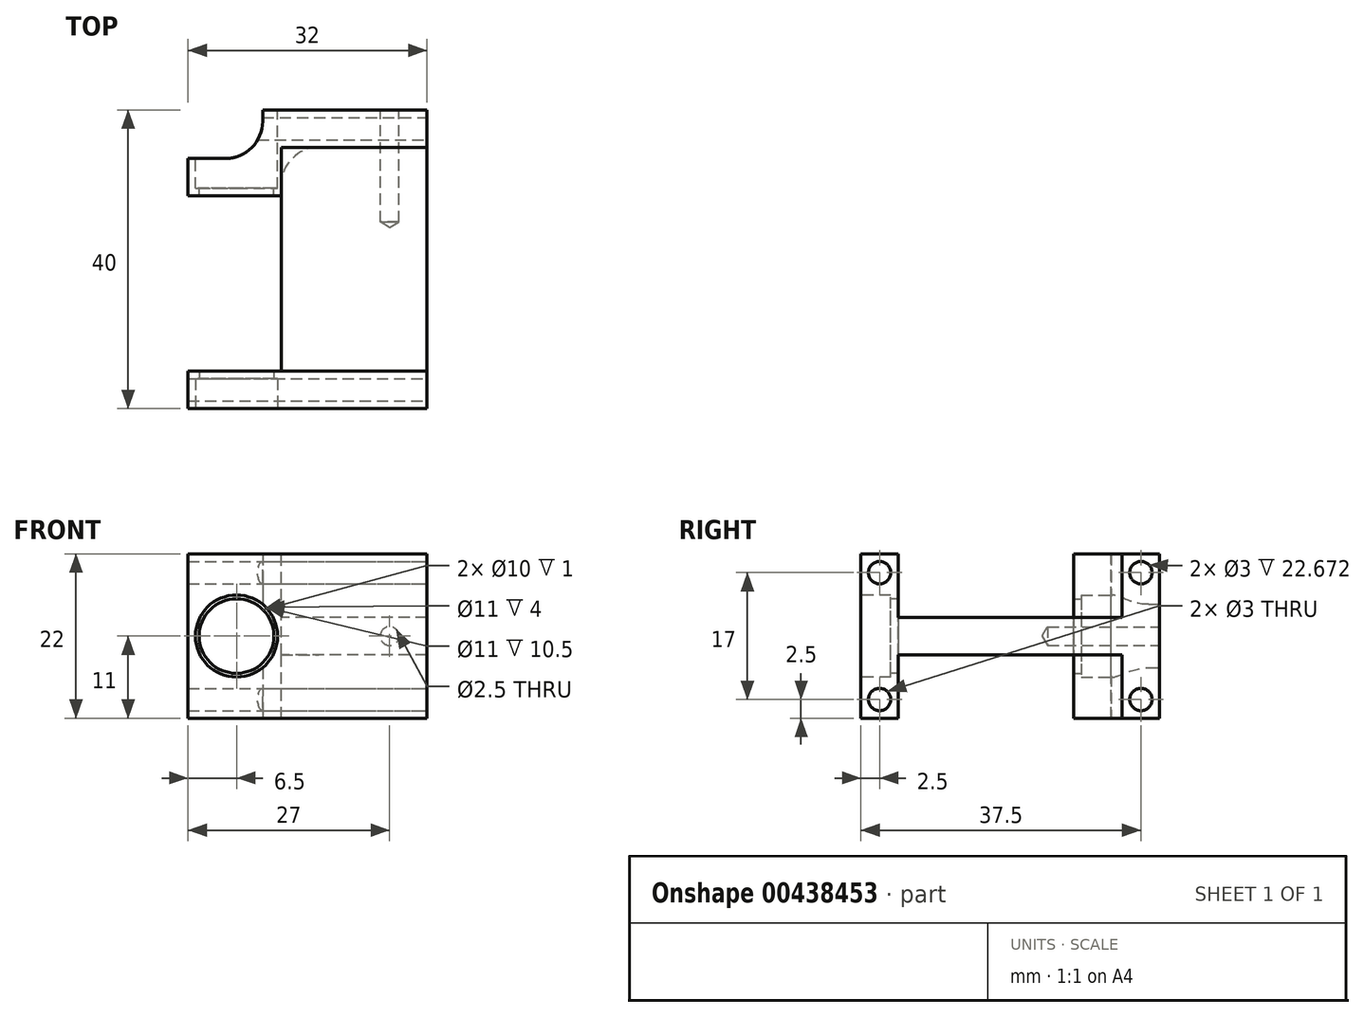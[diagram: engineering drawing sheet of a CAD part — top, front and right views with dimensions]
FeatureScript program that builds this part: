
annotation { "Feature Type Name" : "Feature", "Feature Type Description" : "" }
export const myFeature = defineFeature(function(context is Context, id is Id, definition is map)
    precondition{}
    {
        {
            var Q0;
            Q0=qCreatedBy(makeId("Right.planeOp"),FACE);
            var sketch = newSketch(context, id + "F0", { "sketchPlane" : qUnion([Q0])});
            skLineSegment(sketch, "E0.bottom", {"start": v(20, 2.5) * mm, "end": v(-20, 2.5) * mm});
            skLineSegment(sketch, "E0.top", {"start": v(20, -2.5) * mm, "end": v(-20, -2.5) * mm});
            skLineSegment(sketch, "E0.left", {"start": v(20, 2.5) * mm, "end": v(20, -2.5) * mm});
            skLineSegment(sketch, "E0.right", {"start": v(-20, 2.5) * mm, "end": v(-20, -2.5) * mm});
            skPoint(sketch, "E0.middle", {"position": v(0, 0) * mm});
            skLineSegment(sketch, "E1.bottom", {"start": v(-20, 11) * mm, "end": v(-15, 11) * mm});
            skLineSegment(sketch, "E1.top", {"start": v(-20, -11) * mm, "end": v(-15, -11) * mm});
            skLineSegment(sketch, "E1.left", {"start": v(-20, 11) * mm, "end": v(-20, -11) * mm});
            skLineSegment(sketch, "E1.right", {"start": v(-15, 11) * mm, "end": v(-15, -11) * mm});
            skPoint(sketch, "E2", {"position": v(-20, 0) * mm});
            skPoint(sketch, "E3.MirrorP", {"position": v(20, 0) * mm});
            skLineSegment(sketch, "E4.MirrorCS", {"start": v(15, 11) * mm, "end": v(15, -11) * mm});
            skLineSegment(sketch, "E5.MirrorCS", {"start": v(20, 11) * mm, "end": v(20, -11) * mm});
            skLineSegment(sketch, "E6.MirrorCS", {"start": v(20, 11) * mm, "end": v(15, 11) * mm});
            skLineSegment(sketch, "E7.MirrorCS", {"start": v(20, -11) * mm, "end": v(15, -11) * mm});
            skPoint(sketch, "E8", {"position": v(-17.5, 8.5) * mm});
            skPoint(sketch, "E9", {"position": v(-17.5, 11) * mm});
            skPoint(sketch, "E10.MirrorP", {"position": v(-17.5, -8.5) * mm});
            skPoint(sketch, "E11.MirrorP", {"position": v(17.5, 8.5) * mm});
            skPoint(sketch, "E12.MirrorP", {"position": v(17.5, -8.5) * mm});
            skSolve(sketch);
        }
        {
            var Q0;
            Q0 = qSketchRegion(id + "F0", true);
            extrude(context, id + "F1", {"entities" : qUnion([Q0]), "depth" : 30 * mm});
        }
        {
            var Q0;
            {var subQ5=sQuery(id+"F0.wireOp",EDGE,"E1.bottom");Q0=makeQuery(id+"F0.imprint","IMPRINT",FACE,{"disambiguationData":[TD([[makeQuery(id+"F0.imprint","IMPRINT",EDGE,{"derivedFrom":subQ5}),-1.0]])]});}
            var Q1;
            {var subQ0=sQuery(id+"F0.wireOp",EDGE,"E1.left");var subQ1=sQuery(id+"F0.wireOp",EDGE,"E0.bottom");var subQ2=makeQuery(id+"F0.imprint","INTERSECT",VERTEX,{"derivedFrom":[subQ1,subQ0]});Q1=makeQuery(id+"F0.imprint","IMPRINT",FACE,{"disambiguationData":[TD([[makeQuery(id+"F0.imprint","IMPRINT",EDGE,{"disambiguationData":[TD([[subQ2,1.0]])],"derivedFrom":subQ1}),1.0]])]});}
            var Q2;
            {var subQ5=sQuery(id+"F0.wireOp",EDGE,"E1.top");Q2=makeQuery(id+"F0.imprint","IMPRINT",FACE,{"disambiguationData":[TD([[makeQuery(id+"F0.imprint","IMPRINT",EDGE,{"derivedFrom":subQ5}),1.0]])]});}
            extrude(context, id + "F2", {"entities" : qUnion([Q0, Q1, Q2]), "operationType" : NewBodyOperationType.ADD, "oppositeDirection" : true, "depth" : 2 * mm});
        }
        {
            var Q0;
            Q0=makeQuery(id+"F1.opExtrude","SWEPT_FACE",FACE,{"disambiguationData":[OSD([sQuery(id+"F0.wireOp",EDGE,"E1.left")])]});
            var sketch = newSketch(context, id + "F3", { "sketchPlane" : qUnion([Q0])});
            skCircle(sketch, "E13", {"center": v(4.5, 0) * mm, "radius": 2.5 * mm});
            skCircle(sketch, "E14", {"center": v(4.5, 0) * mm, "radius": 5.5 * mm});
            skCircle(sketch, "E15.0", {"center": v(4.5, 0) * mm, "radius": 5 * mm});
            skSolve(sketch);
        }
        {
            var Q0;
            Q0=makeQuery(id+"F1.opExtrude","SWEPT_FACE",FACE,{"disambiguationData":[OSD([sQuery(id+"F0.wireOp",EDGE,"E0.bottom")])]});
            var sketch = newSketch(context, id + "F4", { "sketchPlane" : qUnion([Q0])});
            skLineSegment(sketch, "E16", {"start": v(4.5, 15) * mm, "end": v(4.5, -15) * mm, "construction": true});
            skLineSegment(sketch, "E17", {"start": v(10.5, 15) * mm, "end": v(10.5, -15) * mm});
            skLineSegment(sketch, "E18", {"start": v(0, 0) * mm, "end": v(30, 0) * mm, "construction": true});
            skSolve(sketch);
        }
        {
            var Q0;
            {var subQ0=sQuery(id+"F4.wireOp",EDGE,"E17");Q0=makeQuery(id+"F4.imprint","IMPRINT",FACE,{"disambiguationData":[TD([[makeQuery(id+"F4.imprint","IMPRINT",EDGE,{"derivedFrom":subQ0}),-1.0]])]});}
            extrude(context, id + "F5", {"entities" : qUnion([Q0]), "operationType" : NewBodyOperationType.REMOVE, "endBound" : BoundingType.THROUGH_ALL, "oppositeDirection" : true, "depth" : 25 * mm});
        }
        {
            var Q0;
            Q0=makeQuery(id+"F3.imprint","IMPRINT",FACE,{"disambiguationData":[TD([[makeQuery(id+"F3.imprint","IMPRINT",EDGE,{"derivedFrom":sQuery(id+"F3.wireOp",EDGE,"E13")}),-1.0]])]});
            var Q1;
            Q1=makeQuery(id+"F3.imprint","IMPRINT",FACE,{"disambiguationData":[TD([[makeQuery(id+"F3.imprint","IMPRINT",EDGE,{"derivedFrom":sQuery(id+"F3.wireOp",EDGE,"E13")}),1.0]])]});
            var Q2;
            Q2=makeQuery(id+"F3.imprint","IMPRINT",FACE,{"disambiguationData":[TD([[makeQuery(id+"F3.imprint","IMPRINT",EDGE,{"derivedFrom":sQuery(id+"F3.wireOp",EDGE,"E14")}),1.0]])]});
            extrude(context, id + "F6", {"entities" : qUnion([Q0, Q1, Q2]), "operationType" : NewBodyOperationType.REMOVE, "oppositeDirection" : true, "depth" : 4 * mm});
        }
        {
            var Q0;
            Q0=makeQuery(id+"F3.imprint","IMPRINT",FACE,{"disambiguationData":[TD([[makeQuery(id+"F3.imprint","IMPRINT",EDGE,{"derivedFrom":sQuery(id+"F3.wireOp",EDGE,"E13")}),1.0]])]});
            var Q1;
            Q1=makeQuery(id+"F3.imprint","IMPRINT",FACE,{"disambiguationData":[TD([[makeQuery(id+"F3.imprint","IMPRINT",EDGE,{"derivedFrom":sQuery(id+"F3.wireOp",EDGE,"E13")}),-1.0]])]});
            var Q2;
            {var subQ0=sQuery(id+"F0.wireOp",EDGE,"E1.right");var subQ1=sQuery(id+"F0.wireOp",EDGE,"E0.bottom");Q2=makeQuery(id+"F5.boolean.opBoolean","MERGE",FACE,{"derivedFrom":[makeQuery(id+"F2.boolean.opBoolean","MERGE",FACE,{"derivedFrom":[makeQuery(id+"F1.opExtrude","SWEPT_FACE",FACE,{"disambiguationData":[OSD([subQ0]),TDD([makeQuery(id+"F0.imprint","IMPRINT",EDGE,{"disambiguationData":[TD([[makeQuery(id+"F0.imprint","INTERSECT",VERTEX,{"derivedFrom":[sQuery(id+"F0.wireOp",EDGE,"E1.bottom"),subQ0]}),-1.0]])],"derivedFrom":subQ0})])]}),makeQuery(id+"F1.opExtrude","SWEPT_FACE",FACE,{"disambiguationData":[OSD([subQ0]),TDD([makeQuery(id+"F0.imprint","IMPRINT",EDGE,{"disambiguationData":[TD([[makeQuery(id+"F0.imprint","INTERSECT",VERTEX,{"derivedFrom":[sQuery(id+"F0.wireOp",EDGE,"E1.top"),subQ0]}),1.0]])],"derivedFrom":subQ0})])]}),makeQuery(id+"F2.opExtrude","SWEPT_FACE",FACE,{"disambiguationData":[OSD([subQ0])]})]}),makeQuery(id+"F5.opExtrude","SWEPT_FACE",FACE,{"disambiguationData":[OSD([subQ1,subQ0])]})]});}
            extrude(context, id + "F7", {"entities" : qUnion([Q0, Q1]), "operationType" : NewBodyOperationType.REMOVE, "endBound" : BoundingType.UP_TO_SURFACE, "oppositeDirection" : true, "endBoundEntityFace" : qUnion([Q2]), "depth" : 25 * mm});
        }
        {
            var Q0;
            Q0=makeQuery(id+"F1.opExtrude","SWEPT_FACE",FACE,{"disambiguationData":[OSD([sQuery(id+"F0.wireOp",EDGE,"E6.MirrorCS")])]});
            var sketch = newSketch(context, id + "F8", { "sketchPlane" : qUnion([Q0])});
            skLineSegment(sketch, "E19.bottom", {"start": v(10.5, 15) * mm, "end": v(-2, 15) * mm});
            skLineSegment(sketch, "E19.top", {"start": v(10.5, 8.5) * mm, "end": v(-2, 8.5) * mm});
            skLineSegment(sketch, "E19.left", {"start": v(10.5, 15) * mm, "end": v(10.5, 8.5) * mm});
            skLineSegment(sketch, "E19.right", {"start": v(-2, 15) * mm, "end": v(-2, 8.5) * mm});
            skSolve(sketch);
        }
        {
            var Q0;
            Q0=makeQuery(id+"F8.imprint","IMPRINT",FACE,{"disambiguationData":[TD([[makeQuery(id+"F8.imprint","IMPRINT",EDGE,{"derivedFrom":sQuery(id+"F8.wireOp",EDGE,"E19.top")}),-1.0]])]});
            var Q1;
            Q1=makeQuery(id+"F1.opExtrude","SWEPT_FACE",FACE,{"disambiguationData":[OSD([sQuery(id+"F0.wireOp",EDGE,"E7.MirrorCS")])]});
            extrude(context, id + "F9", {"entities" : qUnion([Q0]), "operationType" : NewBodyOperationType.ADD, "endBound" : BoundingType.UP_TO_SURFACE, "oppositeDirection" : true, "endBoundEntityFace" : qUnion([Q1]), "depth" : 25 * mm});
        }
        {
            var Q0;
            Q0=makeQuery(id+"F1.opExtrude","CAP_FACE",FACE,{"disambiguationData":[OSD([sQuery(id+"F0.wireOp",EDGE,"E0.bottom"),sQuery(id+"F0.wireOp",EDGE,"E0.top"),sQuery(id+"F0.wireOp",EDGE,"E1.bottom"),sQuery(id+"F0.wireOp",EDGE,"E1.top"),sQuery(id+"F0.wireOp",EDGE,"E1.left"),sQuery(id+"F0.wireOp",EDGE,"E1.right"),sQuery(id+"F0.wireOp",EDGE,"E4.MirrorCS"),sQuery(id+"F0.wireOp",EDGE,"E5.MirrorCS"),sQuery(id+"F0.wireOp",EDGE,"E6.MirrorCS"),sQuery(id+"F0.wireOp",EDGE,"E7.MirrorCS")])],"isStart":true});
            extrude(context, id + "F10", {"entities" : qUnion([Q0]), "operationType" : NewBodyOperationType.REMOVE, "oppositeDirection" : true, "depth" : 8 * mm});
        }
        {
            var Q0;
            Q0=makeQuery(id+"F10.boolean.opBoolean","MERGE",FACE,{"derivedFrom":[makeQuery(id+"F9.opExtrude","SWEPT_FACE",FACE,{"disambiguationData":[OSD([sQuery(id+"F8.wireOp",EDGE,"E19.bottom")])]}),makeQuery(id+"F10.opExtrude","SWEPT_FACE",FACE,{"disambiguationData":[OSD([sQuery(id+"F0.wireOp",EDGE,"E0.bottom"),sQuery(id+"F0.wireOp",EDGE,"E4.MirrorCS")])]})]});
            extrude(context, id + "F11", {"entities" : qUnion([Q0]), "operationType" : NewBodyOperationType.REMOVE, "oppositeDirection" : true, "depth" : 1.5 * mm});
        }
        {
            var Q0;
            Q0=makeQuery(id+"F11.boolean.opBoolean","COPY",EDGE,{"derivedFrom":makeQuery(id+"F11.opExtrude","CAP_EDGE",EDGE,{"disambiguationData":[OSD([sQuery(id+"F0.wireOp",EDGE,"E0.bottom"),sQuery(id+"F0.wireOp",EDGE,"E4.MirrorCS")])],"isStart":false})});
            fillet(context, id + "F12", {"entities" : qUnion([Q0]), "radius" : 5 * mm, "tangentPropagation" : true, "allowEdgeOverflow" : false});
        }
        {
            var Q0;
            {var subQ0=sQuery(id+"F0.wireOp",EDGE,"E6.MirrorCS");var subQ1=sQuery(id+"F0.wireOp",EDGE,"E4.MirrorCS");var subQ2=sQuery(id+"F0.wireOp",EDGE,"E0.bottom");var subQ3=sQuery(id+"F8.wireOp",EDGE,"E19.left");var subQ4=sQuery(id+"F8.wireOp",EDGE,"E19.bottom");Q0=makeQuery(id+"F9.boolean.opBoolean","SPLIT",EDGE,{"disambiguationData":[TD([makeQuery(id+"F1.opExtrude","SWEPT_FACE",FACE,{"disambiguationData":[OSD([subQ2])]})])],"derivedFrom":makeQuery(id+"F9.opExtrude","SWEPT_EDGE",EDGE,{"disambiguationData":[OSD([subQ1,subQ0,subQ4,subQ3])]})});}
            var Q1;
            {var subQ1=sQuery(id+"F0.wireOp",EDGE,"E4.MirrorCS");var subQ2=sQuery(id+"F0.wireOp",EDGE,"E0.top");var subQ4=sQuery(id+"F0.wireOp",EDGE,"E6.MirrorCS");var subQ5=sQuery(id+"F8.wireOp",EDGE,"E19.left");Q1=makeQuery(id+"F9.boolean.opBoolean","SPLIT",EDGE,{"disambiguationData":[TD([makeQuery(id+"F1.opExtrude","SWEPT_FACE",FACE,{"disambiguationData":[OSD([subQ2])]})])],"derivedFrom":makeQuery(id+"F9.opExtrude","SWEPT_EDGE",EDGE,{"disambiguationData":[OSD([subQ1,subQ4,sQuery(id+"F8.wireOp",EDGE,"E19.bottom"),subQ5])]})});}
            fillet(context, id + "F13", {"entities" : qUnion([Q0, Q1]), "radius" : 5 * mm, "tangentPropagation" : true, "allowEdgeOverflow" : false});
        }
        {
            var Q0;
            Q0=makeQuery(id+"F1.opExtrude","SWEPT_FACE",FACE,{"disambiguationData":[OSD([sQuery(id+"F0.wireOp",EDGE,"E5.MirrorCS")])]});
            var sketch = newSketch(context, id + "F14", { "sketchPlane" : qUnion([Q0])});
            skCircle(sketch, "E20", {"center": v(-4.5, 0) * mm, "radius": 2.5 * mm});
            skCircle(sketch, "E21", {"center": v(-4.5, 0) * mm, "radius": 5.5 * mm});
            skCircle(sketch, "E22.0", {"center": v(-4.5, 0) * mm, "radius": 5 * mm});
            skSolve(sketch);
        }
        {
            var Q0;
            {var subQ0=sQuery(id+"F14.wireOp",EDGE,"E21");var subQ1=makeQuery(id+"F10.boolean.opBoolean","COPY",EDGE,{"derivedFrom":makeQuery(id+"F10.opExtrude","CAP_EDGE",EDGE,{"disambiguationData":[OSD([sQuery(id+"F0.wireOp",EDGE,"E5.MirrorCS")])],"isStart":false})});var subQ2=makeQuery(id+"F14.imprint","INTERSECT",VERTEX,{"disambiguationData":[OD(0.0)],"derivedFrom":[subQ1,subQ0]});Q0=makeQuery(id+"F14.imprint","IMPRINT",FACE,{"disambiguationData":[TD([[makeQuery(id+"F14.imprint","IMPRINT",EDGE,{"disambiguationData":[TD([[subQ2,-1.0]])],"derivedFrom":subQ0}),1.0]])]});}
            var Q1;
            {var subQ0=sQuery(id+"F14.wireOp",EDGE,"E21");var subQ1=makeQuery(id+"F10.boolean.opBoolean","COPY",EDGE,{"derivedFrom":makeQuery(id+"F10.opExtrude","CAP_EDGE",EDGE,{"disambiguationData":[OSD([sQuery(id+"F0.wireOp",EDGE,"E5.MirrorCS")])],"isStart":false})});var subQ2=makeQuery(id+"F14.imprint","INTERSECT",VERTEX,{"disambiguationData":[OD(0.0)],"derivedFrom":[subQ1,subQ0]});Q1=makeQuery(id+"F14.imprint","IMPRINT",FACE,{"disambiguationData":[TD([[makeQuery(id+"F14.imprint","IMPRINT",EDGE,{"disambiguationData":[TD([[subQ2,1.0]])],"derivedFrom":subQ0}),1.0]])]});}
            var Q2;
            {var subQ0=sQuery(id+"F14.wireOp",EDGE,"E20");var subQ1=makeQuery(id+"F10.boolean.opBoolean","COPY",EDGE,{"derivedFrom":makeQuery(id+"F10.opExtrude","CAP_EDGE",EDGE,{"disambiguationData":[OSD([sQuery(id+"F0.wireOp",EDGE,"E5.MirrorCS")])],"isStart":false})});var subQ2=makeQuery(id+"F14.imprint","INTERSECT",VERTEX,{"disambiguationData":[OD(0.0)],"derivedFrom":[subQ1,subQ0]});Q2=makeQuery(id+"F14.imprint","IMPRINT",FACE,{"disambiguationData":[TD([[makeQuery(id+"F14.imprint","IMPRINT",EDGE,{"disambiguationData":[TD([[subQ2,-1.0]])],"derivedFrom":subQ0}),-1.0]])]});}
            var Q3;
            {var subQ0=sQuery(id+"F14.wireOp",EDGE,"E20");var subQ1=makeQuery(id+"F10.boolean.opBoolean","COPY",EDGE,{"derivedFrom":makeQuery(id+"F10.opExtrude","CAP_EDGE",EDGE,{"disambiguationData":[OSD([sQuery(id+"F0.wireOp",EDGE,"E5.MirrorCS")])],"isStart":false})});var subQ2=makeQuery(id+"F14.imprint","INTERSECT",VERTEX,{"disambiguationData":[OD(0.0)],"derivedFrom":[subQ1,subQ0]});Q3=makeQuery(id+"F14.imprint","IMPRINT",FACE,{"disambiguationData":[TD([[makeQuery(id+"F14.imprint","IMPRINT",EDGE,{"disambiguationData":[TD([[subQ2,-1.0]])],"derivedFrom":subQ0}),1.0]])]});}
            var Q4;
            {var subQ0=sQuery(id+"F14.wireOp",EDGE,"E20");var subQ1=makeQuery(id+"F10.boolean.opBoolean","COPY",EDGE,{"derivedFrom":makeQuery(id+"F10.opExtrude","CAP_EDGE",EDGE,{"disambiguationData":[OSD([sQuery(id+"F0.wireOp",EDGE,"E5.MirrorCS")])],"isStart":false})});var subQ2=makeQuery(id+"F14.imprint","INTERSECT",VERTEX,{"disambiguationData":[OD(0.0)],"derivedFrom":[subQ1,subQ0]});Q4=makeQuery(id+"F14.imprint","IMPRINT",FACE,{"disambiguationData":[TD([[makeQuery(id+"F14.imprint","IMPRINT",EDGE,{"disambiguationData":[TD([[subQ2,1.0]])],"derivedFrom":subQ0}),1.0]])]});}
            var Q5;
            {var subQ0=sQuery(id+"F14.wireOp",EDGE,"E20");var subQ1=makeQuery(id+"F10.boolean.opBoolean","COPY",EDGE,{"derivedFrom":makeQuery(id+"F10.opExtrude","CAP_EDGE",EDGE,{"disambiguationData":[OSD([sQuery(id+"F0.wireOp",EDGE,"E5.MirrorCS")])],"isStart":false})});var subQ2=makeQuery(id+"F14.imprint","INTERSECT",VERTEX,{"disambiguationData":[OD(0.0)],"derivedFrom":[subQ1,subQ0]});Q5=makeQuery(id+"F14.imprint","IMPRINT",FACE,{"disambiguationData":[TD([[makeQuery(id+"F14.imprint","IMPRINT",EDGE,{"disambiguationData":[TD([[subQ2,1.0]])],"derivedFrom":subQ0}),-1.0]])]});}
            extrude(context, id + "F15", {"entities" : qUnion([Q0, Q1, Q2, Q3, Q4, Q5]), "operationType" : NewBodyOperationType.REMOVE, "oppositeDirection" : true, "depth" : 10.5 * mm});
        }
        {
            var Q0;
            {var subQ0=sQuery(id+"F14.wireOp",EDGE,"E22.0");var subQ1=makeQuery(id+"F12.opFillet","BLEND_EDGE",EDGE,{"blendedFrom":[makeQuery(id+"F10.boolean.opBoolean","COPY",EDGE,{"derivedFrom":makeQuery(id+"F10.opExtrude","CAP_EDGE",EDGE,{"disambiguationData":[OSD([sQuery(id+"F0.wireOp",EDGE,"E0.bottom"),sQuery(id+"F0.wireOp",EDGE,"E4.MirrorCS")])],"isStart":false})}),makeQuery(id+"F1.opExtrude","SWEPT_FACE",FACE,{"disambiguationData":[OSD([sQuery(id+"F0.wireOp",EDGE,"E5.MirrorCS")])]})],"blendedInto":[makeQuery(id+"F1.opExtrude","SWEPT_FACE",FACE,{"disambiguationData":[OSD([sQuery(id+"F0.wireOp",EDGE,"E5.MirrorCS")])]})]});var subQ2=makeQuery(id+"F14.imprint","INTERSECT",VERTEX,{"disambiguationData":[OD(0.0)],"derivedFrom":[subQ1,subQ0]});Q0=makeQuery(id+"F14.imprint","IMPRINT",FACE,{"disambiguationData":[TD([[makeQuery(id+"F14.imprint","IMPRINT",EDGE,{"disambiguationData":[TD([[subQ2,-1.0]])],"derivedFrom":subQ0}),1.0]])]});}
            var Q1;
            Q1=makeQuery(id+"F14.imprint","IMPRINT",FACE,{"disambiguationData":[TD([[makeQuery(id+"F14.imprint","IMPRINT",EDGE,{"derivedFrom":sQuery(id+"F14.wireOp",EDGE,"E20")}),-1.0]])]});
            var Q2;
            Q2=makeQuery(id+"F14.imprint","IMPRINT",FACE,{"disambiguationData":[TD([[makeQuery(id+"F14.imprint","IMPRINT",EDGE,{"derivedFrom":sQuery(id+"F14.wireOp",EDGE,"E20")}),1.0]])]});
            var Q3;
            Q3=makeQuery(id+"F9.opExtrude","SWEPT_FACE",FACE,{"disambiguationData":[OSD([sQuery(id+"F8.wireOp",EDGE,"E19.top")])]});
            extrude(context, id + "F16", {"entities" : qUnion([Q0, Q1, Q2]), "operationType" : NewBodyOperationType.REMOVE, "endBound" : BoundingType.UP_TO_SURFACE, "oppositeDirection" : true, "endBoundEntityFace" : qUnion([Q3]), "depth" : 25 * mm});
        }
        {
            var Q0;
            Q0=makeQuery(id+"F1.opExtrude","CAP_FACE",FACE,{"disambiguationData":[OSD([sQuery(id+"F0.wireOp",EDGE,"E0.bottom"),sQuery(id+"F0.wireOp",EDGE,"E0.top"),sQuery(id+"F0.wireOp",EDGE,"E1.bottom"),sQuery(id+"F0.wireOp",EDGE,"E1.top"),sQuery(id+"F0.wireOp",EDGE,"E1.left"),sQuery(id+"F0.wireOp",EDGE,"E1.right"),sQuery(id+"F0.wireOp",EDGE,"E4.MirrorCS"),sQuery(id+"F0.wireOp",EDGE,"E5.MirrorCS"),sQuery(id+"F0.wireOp",EDGE,"E6.MirrorCS"),sQuery(id+"F0.wireOp",EDGE,"E7.MirrorCS")])],"isStart":false});
            var sketch = newSketch(context, id + "F17", { "sketchPlane" : qUnion([Q0])});
            skPoint(sketch, "E23", {"position": v(-17.5, 8.5) * mm});
            skPoint(sketch, "E24.MirrorP", {"position": v(-17.5, -8.5) * mm});
            skPoint(sketch, "E25.MirrorP", {"position": v(17.5, -8.5) * mm});
            skPoint(sketch, "E26.MirrorP", {"position": v(17.5, 8.5) * mm});
            skSolve(sketch);
        }
        {
            var Q0;
            Q0=sQuery(id+"F17.wireOp",VERTEX,"E23");
            var Q1;
            Q1=sQuery(id+"F17.wireOp",VERTEX,"E24.MirrorP");
            var Q2;
            Q2=sQuery(id+"F17.wireOp",VERTEX,"E26.MirrorP");
            var Q3;
            Q3=sQuery(id+"F17.wireOp",VERTEX,"E25.MirrorP");
            var Q4;
            Q4=makeQuery(id+"F1.opExtrude","SWEPT_BODY",BODY,{"disambiguationData":[OSD([sQuery(id+"F0.wireOp",EDGE,"E0.bottom"),sQuery(id+"F0.wireOp",EDGE,"E0.top"),sQuery(id+"F0.wireOp",EDGE,"E1.bottom"),sQuery(id+"F0.wireOp",EDGE,"E1.top"),sQuery(id+"F0.wireOp",EDGE,"E1.left"),sQuery(id+"F0.wireOp",EDGE,"E1.right"),sQuery(id+"F0.wireOp",EDGE,"E4.MirrorCS"),sQuery(id+"F0.wireOp",EDGE,"E5.MirrorCS"),sQuery(id+"F0.wireOp",EDGE,"E6.MirrorCS"),sQuery(id+"F0.wireOp",EDGE,"E7.MirrorCS")])]});
            hole(context, id + "F18", {"style" : HoleStyle.SIMPLE, "endStyle" : HoleEndStyle.THROUGH, "holeDiameter" : 3 * mm, "isTappedThrough" : true, "tappedDepth" : 12 * mm, "tapClearance" : 3, "locations" : qUnion([Q0, Q1, Q2, Q3]), "scope" : qUnion([Q4])});
        }
        {
            var Q0;
            {var subQ1=sQuery(id+"F0.wireOp",EDGE,"E6.MirrorCS");var subQ2=sQuery(id+"F0.wireOp",EDGE,"E5.MirrorCS");Q0=makeQuery(id+"F15.boolean.opBoolean","SPLIT",FACE,{"disambiguationData":[TD([makeQuery(id+"F1.opExtrude","SWEPT_FACE",FACE,{"disambiguationData":[OSD([subQ1])]})])],"derivedFrom":makeQuery(id+"F1.opExtrude","SWEPT_FACE",FACE,{"disambiguationData":[OSD([subQ2])]})});}
            var sketch = newSketch(context, id + "F19", { "sketchPlane" : qUnion([Q0])});
            skPoint(sketch, "E27", {"position": v(-25, 0) * mm});
            skSolve(sketch);
        }
        {
            var Q0;
            Q0=sQuery(id+"F19.wireOp",VERTEX,"E27");
            var Q1;
            Q1=makeQuery(id+"F1.opExtrude","SWEPT_BODY",BODY,{"disambiguationData":[OSD([sQuery(id+"F0.wireOp",EDGE,"E0.bottom"),sQuery(id+"F0.wireOp",EDGE,"E0.top"),sQuery(id+"F0.wireOp",EDGE,"E1.bottom"),sQuery(id+"F0.wireOp",EDGE,"E1.top"),sQuery(id+"F0.wireOp",EDGE,"E1.left"),sQuery(id+"F0.wireOp",EDGE,"E1.right"),sQuery(id+"F0.wireOp",EDGE,"E4.MirrorCS"),sQuery(id+"F0.wireOp",EDGE,"E5.MirrorCS"),sQuery(id+"F0.wireOp",EDGE,"E6.MirrorCS"),sQuery(id+"F0.wireOp",EDGE,"E7.MirrorCS")])]});
            hole(context, id + "F20", {"style" : HoleStyle.SIMPLE, "endStyle" : HoleEndStyle.BLIND, "holeDiameter" : 2.5 * mm, "holeDepth" : 15 * mm, "isTappedThrough" : true, "tappedDepth" : 12 * mm, "tapClearance" : 3, "locations" : qUnion([Q0]), "scope" : qUnion([Q1])});
        }
    });
